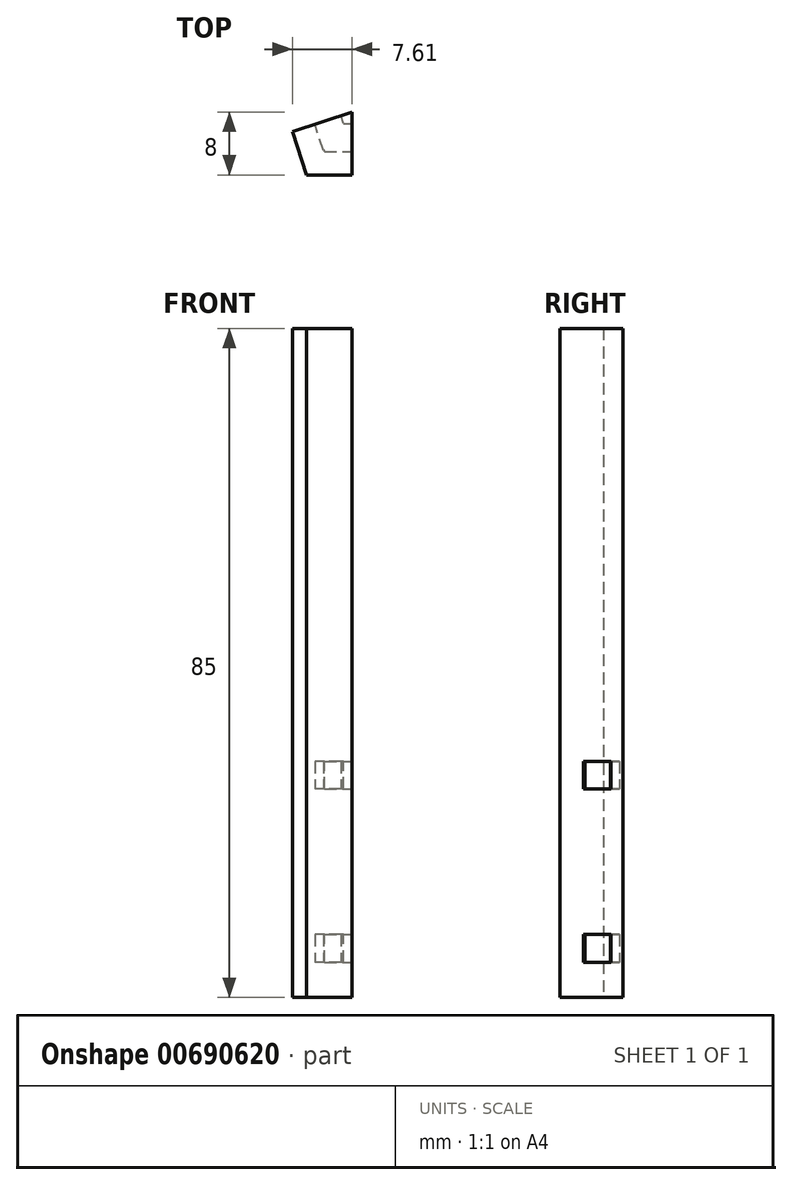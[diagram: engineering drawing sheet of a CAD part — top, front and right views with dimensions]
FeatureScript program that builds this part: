
annotation { "Feature Type Name" : "Feature", "Feature Type Description" : "" }
export const myFeature = defineFeature(function(context is Context, id is Id, definition is map)
    precondition{}
    {
        {
            var Q0;
            Q0=qCreatedBy(makeId("Top.planeOp"),FACE);
            var sketch = newSketch(context, id + "F0", { "sketchPlane" : qUnion([Q0])});
            skCircle(sketch, "E0.cCircle", {"center": v(0, 0) * mm, "radius": 34.4 * mm, "construction": true});
            skLineSegment(sketch, "E0.0", {"start": v(25, -34.4) * mm, "end": v(-25, -34.4) * mm});
            skLineSegment(sketch, "E0.1", {"start": v(-25, -34.4) * mm, "end": v(-40.45, 13.14) * mm});
            skLineSegment(sketch, "E0.2", {"start": v(-40.45, 13.14) * mm, "end": v(0, 42.53) * mm});
            skLineSegment(sketch, "E0.3", {"start": v(0, 42.53) * mm, "end": v(40.45, 13.14) * mm});
            skLineSegment(sketch, "E0.4", {"start": v(40.45, 13.14) * mm, "end": v(25, -34.4) * mm});
            skPoint(sketch, "E0.0.midPoint", {"position": v(0, -34.4) * mm});
            skLineSegment(sketch, "E1.0", {"start": v(48.06, 10.67) * mm, "end": v(32.6, -36.88) * mm});
            skLineSegment(sketch, "E2.0", {"start": v(25, -42.4) * mm, "end": v(-25, -42.4) * mm});
            skLineSegment(sketch, "E3", {"start": v(25, -34.4) * mm, "end": v(25, -42.4) * mm});
            skLineSegment(sketch, "E4", {"start": v(25, -34.4) * mm, "end": v(32.6, -36.88) * mm});
            skLineSegment(sketch, "E5", {"start": v(25, -42.4) * mm, "end": v(30.81, -42.4) * mm});
            skLineSegment(sketch, "E6", {"start": v(32.6, -36.88) * mm, "end": v(30.81, -42.4) * mm});
            skLineSegment(sketch, "E7.1.0", {"start": v(40.45, 13.14) * mm, "end": v(48.06, 10.67) * mm});
            skLineSegment(sketch, "E7.1.1", {"start": v(40.45, 13.14) * mm, "end": v(45.15, 19.62) * mm});
            skLineSegment(sketch, "E7.1.2", {"start": v(45.15, 19.62) * mm, "end": v(49.86, 16.2) * mm});
            skLineSegment(sketch, "E7.1.3", {"start": v(48.06, 10.67) * mm, "end": v(49.86, 16.2) * mm});
            skLineSegment(sketch, "E7.2.0", {"start": v(0, 42.53) * mm, "end": v(4.7, 49) * mm});
            skLineSegment(sketch, "E7.2.1", {"start": v(0, 42.53) * mm, "end": v(-4.7, 49) * mm});
            skLineSegment(sketch, "E7.2.2", {"start": v(-4.7, 49) * mm, "end": v(0, 52.42) * mm});
            skLineSegment(sketch, "E7.2.3", {"start": v(4.7, 49) * mm, "end": v(0, 52.42) * mm});
            skLineSegment(sketch, "E7.3.0", {"start": v(-40.45, 13.14) * mm, "end": v(-45.15, 19.62) * mm});
            skLineSegment(sketch, "E7.3.1", {"start": v(-40.45, 13.14) * mm, "end": v(-48.06, 10.67) * mm});
            skLineSegment(sketch, "E7.3.2", {"start": v(-48.06, 10.67) * mm, "end": v(-49.86, 16.2) * mm});
            skLineSegment(sketch, "E7.3.3", {"start": v(-45.15, 19.62) * mm, "end": v(-49.86, 16.2) * mm});
            skLineSegment(sketch, "E7.4.0", {"start": v(-25, -34.4) * mm, "end": v(-32.6, -36.88) * mm});
            skLineSegment(sketch, "E7.4.1", {"start": v(-25, -34.4) * mm, "end": v(-25, -42.4) * mm});
            skLineSegment(sketch, "E7.4.2", {"start": v(-25, -42.4) * mm, "end": v(-30.81, -42.4) * mm});
            skLineSegment(sketch, "E7.4.3", {"start": v(-32.6, -36.88) * mm, "end": v(-30.81, -42.4) * mm});
            skSolve(sketch);
        }
        {
            var Q0;
            Q0=makeQuery(id+"F0.imprint","IMPRINT",FACE,{"disambiguationData":[TD([[makeQuery(id+"F0.imprint","IMPRINT",EDGE,{"derivedFrom":sQuery(id+"F0.wireOp",EDGE,"E7.4.0")}),1.0]])]});
            extrude(context, id + "F1", {"entities" : qUnion([Q0]), "depth" : 85 * mm, "offsetDistance" : 25 * mm});
        }
        {
            var Q0;
            Q0=makeQuery(id+"F1.opExtrude","SWEPT_FACE",FACE,{"disambiguationData":[OSD([sQuery(id+"F0.wireOp",EDGE,"E7.4.1")])]});
            var sketch = newSketch(context, id + "F2", { "sketchPlane" : qUnion([Q0])});
            skLineSegment(sketch, "E8.bottom", {"start": v(-39.4, 8) * mm, "end": v(-35.9, 8) * mm});
            skLineSegment(sketch, "E8.top", {"start": v(-39.4, 4.5) * mm, "end": v(-35.9, 4.5) * mm});
            skLineSegment(sketch, "E8.left", {"start": v(-39.4, 8) * mm, "end": v(-39.4, 4.5) * mm});
            skLineSegment(sketch, "E8.right", {"start": v(-35.9, 8) * mm, "end": v(-35.9, 4.5) * mm});
            skLineSegment(sketch, "E9.bottom", {"start": v(-39.4, 30) * mm, "end": v(-35.9, 30) * mm});
            skLineSegment(sketch, "E9.top", {"start": v(-39.4, 26.5) * mm, "end": v(-35.9, 26.5) * mm});
            skLineSegment(sketch, "E9.left", {"start": v(-39.4, 30) * mm, "end": v(-39.4, 26.5) * mm});
            skLineSegment(sketch, "E9.right", {"start": v(-35.9, 30) * mm, "end": v(-35.9, 26.5) * mm});
            skSolve(sketch);
        }
        {
            var Q0;
            Q0=makeQuery(id+"F2.imprint","IMPRINT",FACE,{"disambiguationData":[TD([[makeQuery(id+"F2.imprint","IMPRINT",EDGE,{"derivedFrom":sQuery(id+"F2.wireOp",EDGE,"E8.bottom")}),-1.0]])]});
            var Q1;
            Q1=makeQuery(id+"F2.imprint","IMPRINT",FACE,{"disambiguationData":[TD([[makeQuery(id+"F2.imprint","IMPRINT",EDGE,{"derivedFrom":sQuery(id+"F2.wireOp",EDGE,"E9.bottom")}),-1.0]])]});
            extrude(context, id + "F3", {"entities" : qUnion([Q0, Q1]), "operationType" : NewBodyOperationType.REMOVE, "oppositeDirection" : true, "depth" : 3.5 * mm, "offsetDistance" : 25 * mm});
        }
        {
            var Q0;
            Q0=makeQuery(id+"F1.opExtrude","SWEPT_FACE",FACE,{"disambiguationData":[OSD([sQuery(id+"F0.wireOp",EDGE,"E7.4.0")])]});
            var sketch = newSketch(context, id + "F4", { "sketchPlane" : qUnion([Q0])});
            skLineSegment(sketch, "E10.bottom", {"start": v(35.9, 8) * mm, "end": v(39.4, 8) * mm});
            skLineSegment(sketch, "E10.top", {"start": v(35.9, 4.5) * mm, "end": v(39.4, 4.5) * mm});
            skLineSegment(sketch, "E10.left", {"start": v(35.9, 8) * mm, "end": v(35.9, 4.5) * mm});
            skLineSegment(sketch, "E10.right", {"start": v(39.4, 8) * mm, "end": v(39.4, 4.5) * mm});
            skLineSegment(sketch, "E11.bottom", {"start": v(35.9, 30) * mm, "end": v(39.4, 30) * mm});
            skLineSegment(sketch, "E11.top", {"start": v(35.9, 26.5) * mm, "end": v(39.4, 26.5) * mm});
            skLineSegment(sketch, "E11.left", {"start": v(35.9, 30) * mm, "end": v(35.9, 26.5) * mm});
            skLineSegment(sketch, "E11.right", {"start": v(39.4, 30) * mm, "end": v(39.4, 26.5) * mm});
            skSolve(sketch);
        }
        {
            var Q0;
            Q0 = qSketchRegion(id + "F4", true);
            extrude(context, id + "F5", {"entities" : qUnion([Q0]), "operationType" : NewBodyOperationType.REMOVE, "oppositeDirection" : true, "depth" : 3.5 * mm, "offsetDistance" : 25 * mm});
        }
    });
